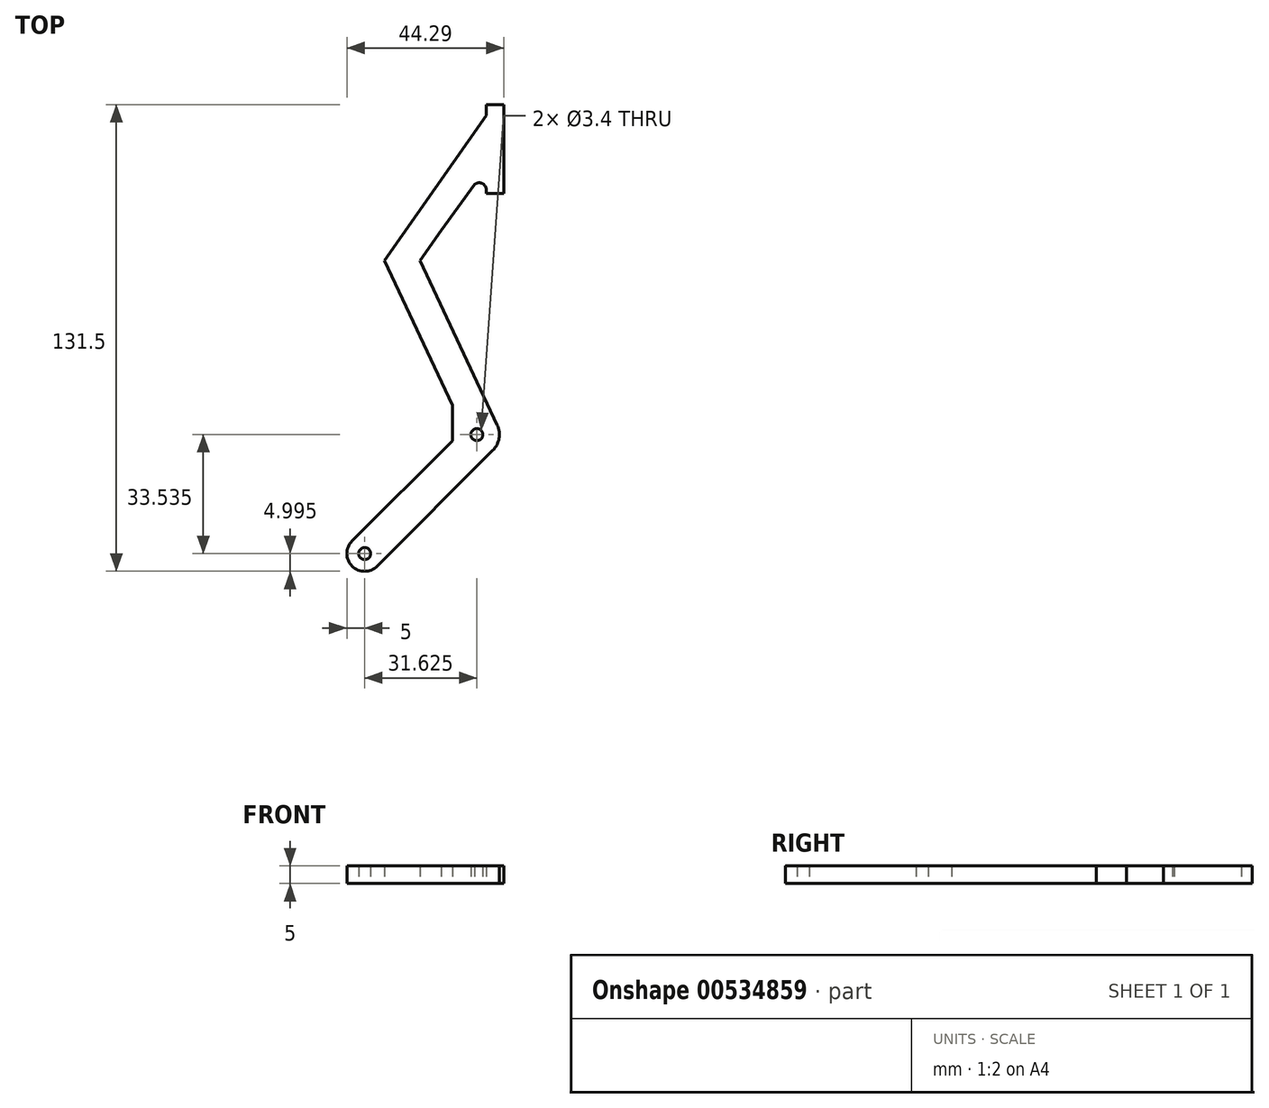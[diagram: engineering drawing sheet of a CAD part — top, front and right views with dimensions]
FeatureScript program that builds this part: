
annotation { "Feature Type Name" : "Feature", "Feature Type Description" : "" }
export const myFeature = defineFeature(function(context is Context, id is Id, definition is map)
    precondition{}
    {
        {
            var Q0;
            Q0=qCreatedBy(makeId("Top.planeOp"),FACE);
            var sketch = newSketch(context, id + "F0", { "sketchPlane" : qUnion([Q0])});
            skLineSegment(sketch, "E0", {"start": v(28.64, 109.53) * mm, "end": v(33.64, 109.53) * mm});
            skLineSegment(sketch, "E1", {"start": v(33.64, 109.53) * mm, "end": v(33.64, 84.53) * mm});
            skLineSegment(sketch, "E2", {"start": v(33.64, 84.53) * mm, "end": v(28.64, 84.53) * mm});
            skLineSegment(sketch, "E3", {"start": v(28.64, 109.53) * mm, "end": v(28.64, 106.53) * mm});
            skLineSegment(sketch, "E4", {"start": v(28.64, 84.53) * mm, "end": v(28.64, 85.53) * mm});
            skLineSegment(sketch, "E5", {"start": v(28.64, 106.53) * mm, "end": v(-0.04, 65.57) * mm});
            skLineSegment(sketch, "E6", {"start": v(-0.04, 65.57) * mm, "end": v(19.1, 24.85) * mm});
            skLineSegment(sketch, "E7", {"start": v(9.96, 65.57) * mm, "end": v(31.72, 19.26) * mm});
            skLineSegment(sketch, "E8", {"start": v(19.1, 24.85) * mm, "end": v(19.1, 14.85) * mm});
            skLineSegment(sketch, "E9", {"start": v(19.1, 14.85) * mm, "end": v(-9.19, -13.44) * mm});
            skLineSegment(sketch, "E10", {"start": v(9.96, 65.57) * mm, "end": v(15.97, 74.15) * mm});
            skArc(sketch, "E11", {"start": v(28.64, 85.53) * mm, "mid": v(27.47, 87.35) * mm, "end": v(25.33, 87.04) * mm});
            skLineSegment(sketch, "E12", {"start": v(15.97, 74.15) * mm, "end": v(25.33, 87.04) * mm});
            skLineSegment(sketch, "E13", {"start": v(19.1, 14.85) * mm, "end": v(26.17, 7.77) * mm});
            skLineSegment(sketch, "E14", {"start": v(26.17, 7.77) * mm, "end": v(30.47, 12.07) * mm});
            skPoint(sketch, "E15.newPointA", {"position": v(35.48, 11.27) * mm});
            skArc(sketch, "E15.filletArc", {"start": v(30.47, 12.07) * mm, "mid": v(32.23, 15.47) * mm, "end": v(31.72, 19.26) * mm});
            skCircle(sketch, "E16", {"center": v(25.98, 16.56) * mm, "radius": 1.7 * mm});
            skLineSegment(sketch, "E17", {"start": v(26.17, 7.77) * mm, "end": v(-2.11, -20.51) * mm});
            skLineSegment(sketch, "E18", {"start": v(-2.11, -20.51) * mm, "end": v(-9.19, -13.44) * mm});
            skArc(sketch, "E19", {"start": v(-9.19, -13.44) * mm, "mid": v(-9.19, -20.51) * mm, "end": v(-2.11, -20.51) * mm});
            skCircle(sketch, "E20", {"center": v(-5.65, -16.97) * mm, "radius": 1.7 * mm});
            skSolve(sketch);
        }
        {
            var Q0;
            Q0=qSketchRegion(id+"F0",true);
            extrude(context, id + "F1", {"entities" : qUnion([Q0]), "depth" : 5 * mm});
        }
    });
